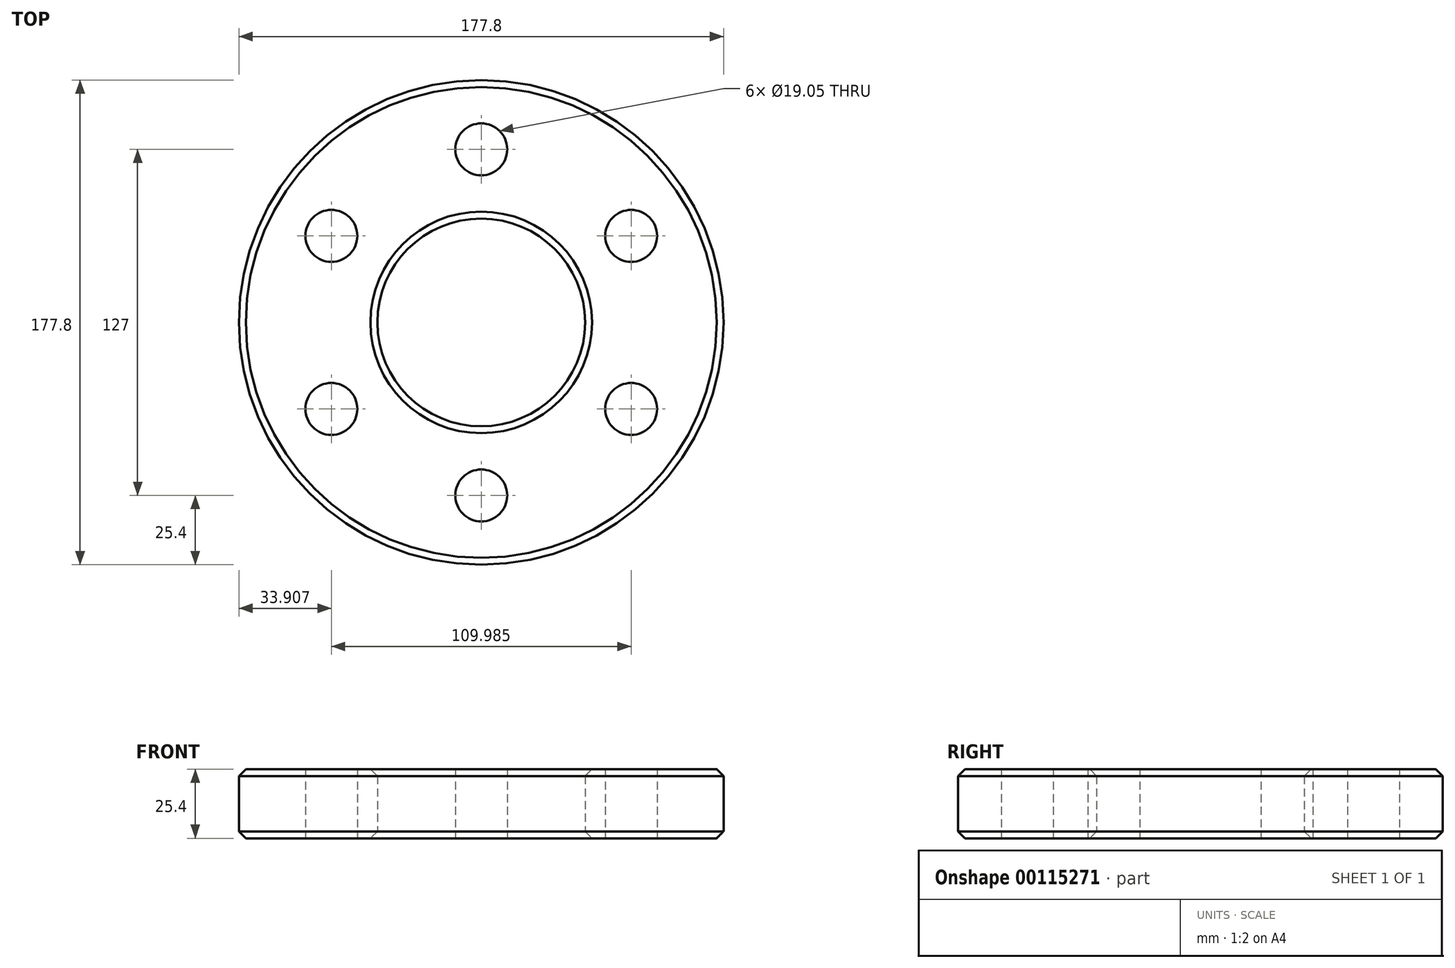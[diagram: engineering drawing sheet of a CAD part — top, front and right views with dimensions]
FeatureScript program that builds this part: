
annotation { "Feature Type Name" : "Feature", "Feature Type Description" : "" }
export const myFeature = defineFeature(function(context is Context, id is Id, definition is map)
    precondition{}
    {
        {
            var Q0;
            Q0=qCreatedBy(makeId("Top.planeOp"),FACE);
            var sketch = newSketch(context, id + "F0", { "sketchPlane" : qUnion([Q0])});
            skCircle(sketch, "E0", {"center": v(0, 0) * mm, "radius": 38.1 * mm});
            skCircle(sketch, "E1", {"center": v(0, 0) * mm, "radius": 88.9 * mm});
            skCircle(sketch, "E2", {"center": v(0, 0) * mm, "radius": 63.5 * mm, "construction": true});
            skCircle(sketch, "E3", {"center": v(0, 63.5) * mm, "radius": 9.53 * mm});
            skCircle(sketch, "E4.1.0", {"center": v(-55, 31.75) * mm, "radius": 9.53 * mm});
            skCircle(sketch, "E4.2.0", {"center": v(-55, -31.75) * mm, "radius": 9.53 * mm});
            skCircle(sketch, "E4.3.0", {"center": v(0, -63.5) * mm, "radius": 9.53 * mm});
            skCircle(sketch, "E4.4.0", {"center": v(55, -31.75) * mm, "radius": 9.53 * mm});
            skCircle(sketch, "E4.5.0", {"center": v(55, 31.75) * mm, "radius": 9.53 * mm});
            skSolve(sketch);
        }
        {
            var Q0;
            Q0=makeQuery(id+"F0.imprint","IMPRINT",FACE,{"disambiguationData":[TD([[makeQuery(id+"F0.imprint","IMPRINT",EDGE,{"derivedFrom":sQuery(id+"F0.wireOp",EDGE,"E0")}),-1.0]])]});
            extrude(context, id + "F1", {"entities" : qUnion([Q0]), "depth" : 25.4 * mm});
        }
        {
            var Q0;
            Q0=makeQuery(id+"F1.opExtrude","CAP_EDGE",EDGE,{"disambiguationData":[OSD([sQuery(id+"F0.wireOp",EDGE,"E0")])],"isStart":false});
            var Q1;
            Q1=makeQuery(id+"F1.opExtrude","CAP_EDGE",EDGE,{"disambiguationData":[OSD([sQuery(id+"F0.wireOp",EDGE,"E1")])],"isStart":false});
            var Q2;
            Q2=makeQuery(id+"F1.opExtrude","CAP_EDGE",EDGE,{"disambiguationData":[OSD([sQuery(id+"F0.wireOp",EDGE,"E1")])],"isStart":true});
            var Q3;
            Q3=makeQuery(id+"F1.opExtrude","CAP_EDGE",EDGE,{"disambiguationData":[OSD([sQuery(id+"F0.wireOp",EDGE,"E0")])],"isStart":true});
            chamfer(context, id + "F2", {"entities" : qUnion([Q0, Q1, Q2, Q3]), "width" : 2.54 * mm, "tangentPropagation" : true});
        }
    });
